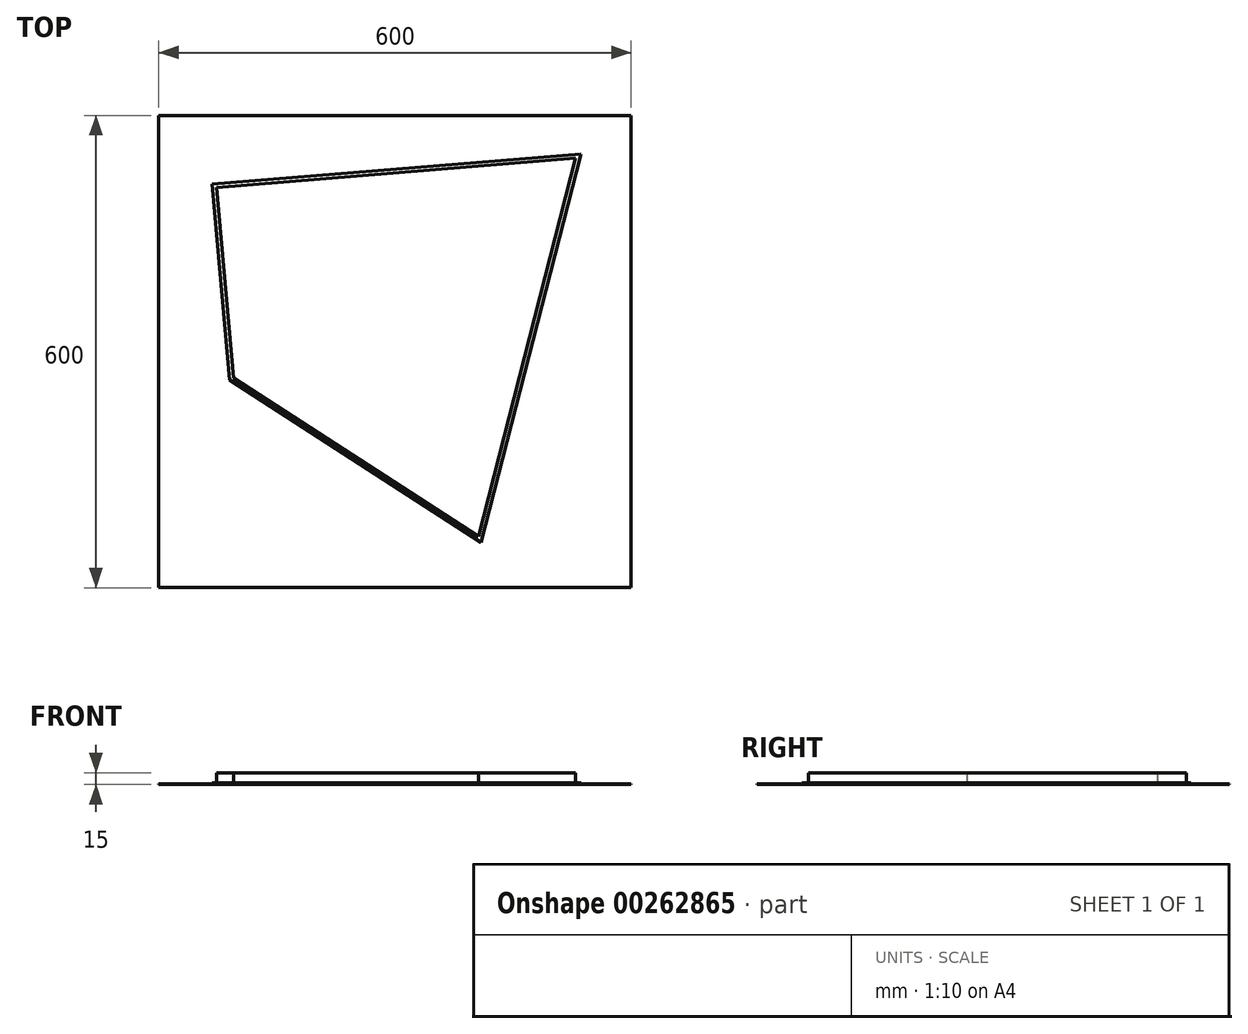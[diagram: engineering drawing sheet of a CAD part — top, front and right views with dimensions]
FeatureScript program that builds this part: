
annotation { "Feature Type Name" : "Feature", "Feature Type Description" : "" }
export const myFeature = defineFeature(function(context is Context, id is Id, definition is map)
    precondition{}
    {
        {
            var Q0;
            Q0=qCreatedBy(makeId("Top.planeOp"),FACE);
            var sketch = newSketch(context, id + "F0", { "sketchPlane" : qUnion([Q0])});
            skLineSegment(sketch, "E0.bottom", {"start": v(310.8, 279.48) * mm, "end": v(-289.2, 279.48) * mm});
            skLineSegment(sketch, "E0.top", {"start": v(310.8, -320.52) * mm, "end": v(-289.2, -320.52) * mm});
            skLineSegment(sketch, "E0.left", {"start": v(310.8, 279.48) * mm, "end": v(310.8, -320.52) * mm});
            skLineSegment(sketch, "E0.right", {"start": v(-289.2, 279.48) * mm, "end": v(-289.2, -320.52) * mm});
            skLineSegment(sketch, "E1", {"start": v(246.93, 230.56) * mm, "end": v(-221.5, 192.18) * mm});
            skLineSegment(sketch, "E2", {"start": v(246.93, 230.56) * mm, "end": v(119.8, -263.34) * mm});
            skLineSegment(sketch, "E3", {"start": v(119.8, -263.34) * mm, "end": v(-199.19, -56.82) * mm});
            skLineSegment(sketch, "E4", {"start": v(-199.19, -56.82) * mm, "end": v(-221.5, 192.18) * mm});
            skPoint(sketch, "E5.middle", {"position": v(99.2, 124.03) * mm});
            skLineSegment(sketch, "E6.0", {"start": v(116.68, -255.37) * mm, "end": v(-194.43, -53.95) * mm});
            skLineSegment(sketch, "E6.1", {"start": v(240.34, 225) * mm, "end": v(116.68, -255.37) * mm});
            skLineSegment(sketch, "E6.2", {"start": v(240.34, 225) * mm, "end": v(-216.07, 187.61) * mm});
            skLineSegment(sketch, "E6.3", {"start": v(-194.43, -53.95) * mm, "end": v(-216.07, 187.61) * mm});
            skSolve(sketch);
        }
        {
            var Q0;
            Q0=makeQuery(id+"F0.imprint","IMPRINT",FACE,{"disambiguationData":[TD([[makeQuery(id+"F0.imprint","IMPRINT",EDGE,{"derivedFrom":sQuery(id+"F0.wireOp",EDGE,"E0.bottom")}),1.0]])]});
            extrude(context, id + "F5", {"entities" : qUnion([Q0]), "depth" : 1 * mm});
        }
        {
            var Q0;
            Q0=makeQuery(id+"F0.imprint","IMPRINT",FACE,{"disambiguationData":[TD([[makeQuery(id+"F0.imprint","IMPRINT",EDGE,{"derivedFrom":sQuery(id+"F0.wireOp",EDGE,"E1")}),1.0]])]});
            extrude(context, id + "F1", {"entities" : qUnion([Q0]), "operationType" : NewBodyOperationType.ADD, "depth" : 2 * mm});
        }
        {
            var Q0;
            Q0=makeQuery(id+"F0.imprint","IMPRINT",FACE,{"disambiguationData":[TD([[makeQuery(id+"F0.imprint","IMPRINT",EDGE,{"derivedFrom":sQuery(id+"F0.wireOp",EDGE,"E6.0")}),-1.0]])]});
            extrude(context, id + "F2", {"entities" : qUnion([Q0]), "operationType" : NewBodyOperationType.ADD, "depth" : 15 * mm});
        }
    });
